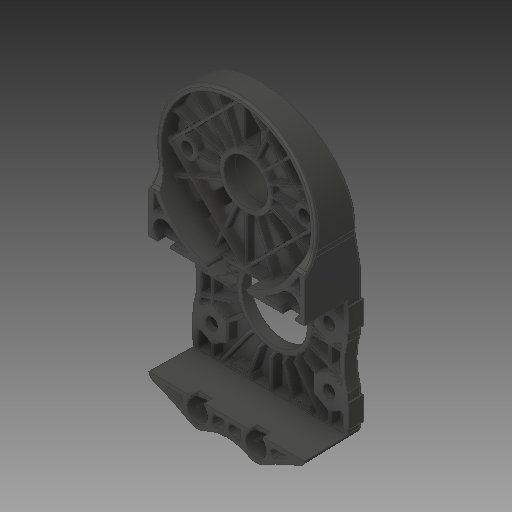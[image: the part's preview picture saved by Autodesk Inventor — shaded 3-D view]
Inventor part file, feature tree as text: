
AUTODESK INVENTOR PART (.ipt)
format: ipt  version: 2017 (Build 210142000, 142)  size: 5,625,856 bytes
history: native  units: in
note: dims shown in document units (in); Inventor stores cm internally (conversion verified against a paired STEP export)
features: chamfer x1
ambient origin geometry x8: Origin, YZ Plane, XZ Plane, XY Plane, X Axis, Y Axis, Z Axis, Center Point
bodies: Solid1 (feature_tree)
feature tree (1):
  chamfer  "Chamfer2"  [1 undecoded]
note: 1 required parameter value undecoded (feature->parameter linkage not recoverable at this tier; creation-order binding heuristic only, values carry confidence <= 0.55)
